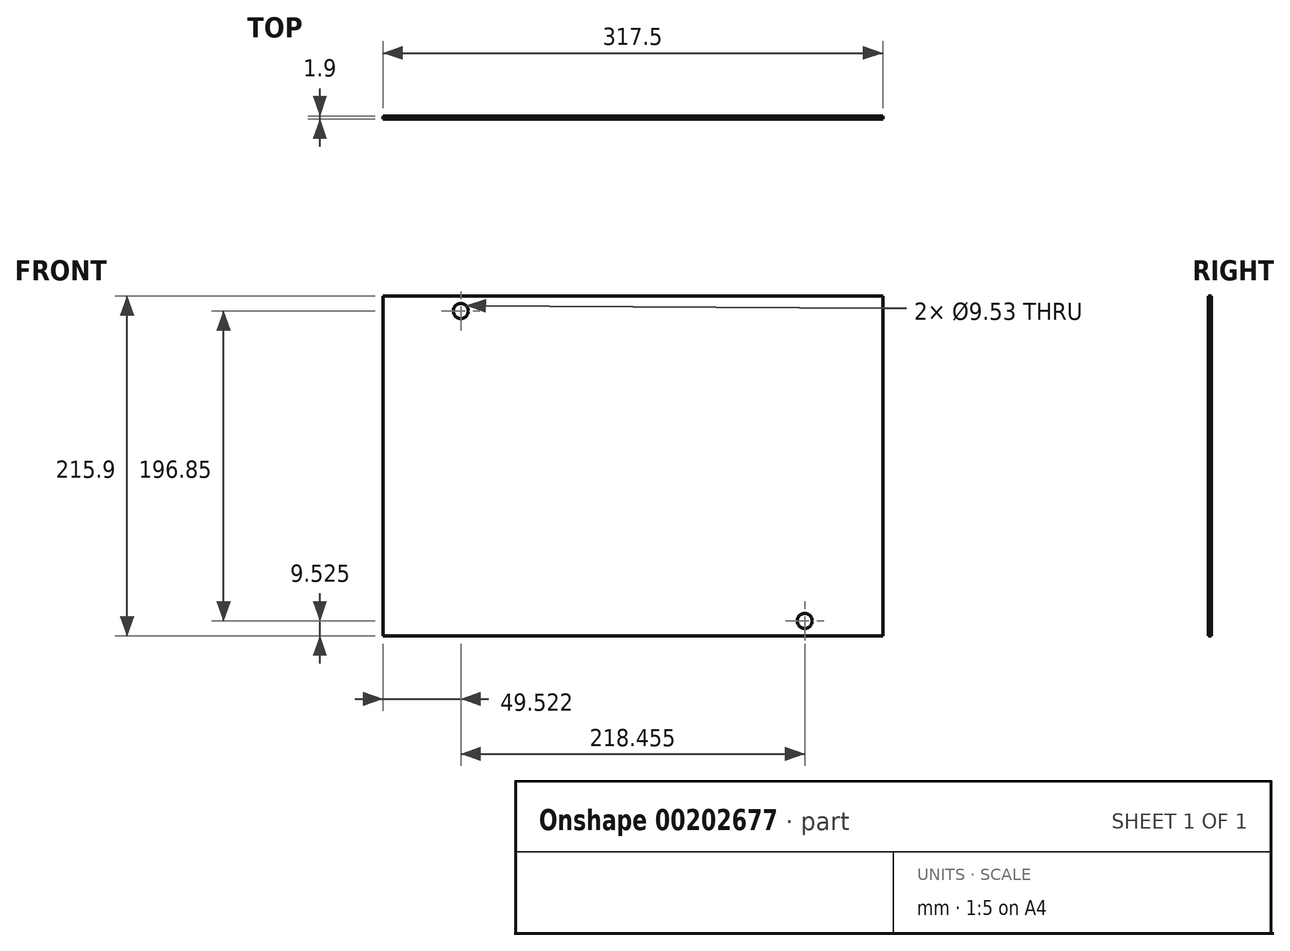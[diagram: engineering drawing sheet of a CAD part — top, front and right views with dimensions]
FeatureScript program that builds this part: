
annotation { "Feature Type Name" : "Feature", "Feature Type Description" : "" }
export const myFeature = defineFeature(function(context is Context, id is Id, definition is map)
    precondition{}
    {
        {
            var Q0;
            Q0=qCreatedBy(makeId("Front.planeOp"),FACE);
            var sketch = newSketch(context, id + "F0", { "sketchPlane" : qUnion([Q0])});
            skLineSegment(sketch, "E0.bottom", {"start": v(-158.75, 107.95) * mm, "end": v(158.75, 107.95) * mm});
            skLineSegment(sketch, "E0.top", {"start": v(-158.75, -107.95) * mm, "end": v(158.75, -107.95) * mm});
            skLineSegment(sketch, "E0.left", {"start": v(-158.75, 107.95) * mm, "end": v(-158.75, -107.95) * mm});
            skLineSegment(sketch, "E0.right", {"start": v(158.75, 107.95) * mm, "end": v(158.75, -107.95) * mm});
            skPoint(sketch, "E0.middle", {"position": v(0, 0) * mm});
            skSolve(sketch);
        }
        {
            var Q0;
            Q0 = qSketchRegion(id + "F0", true);
            extrude(context, id + "F1", {"entities" : qUnion([Q0]), "depth" : 1.9 * mm});
        }
        {
            var Q0;
            Q0=makeQuery(id+"F1.opExtrude","CAP_FACE",FACE,{"disambiguationData":[OSD([sQuery(id+"F0.wireOp",EDGE,"E0.bottom"),sQuery(id+"F0.wireOp",EDGE,"E0.top"),sQuery(id+"F0.wireOp",EDGE,"E0.left"),sQuery(id+"F0.wireOp",EDGE,"E0.right")])],"isStart":false});
            var sketch = newSketch(context, id + "F2", { "sketchPlane" : qUnion([Q0])});
            skCircle(sketch, "E1", {"center": v(-109.23, 98.42) * mm, "radius": 4.76 * mm});
            skCircle(sketch, "E2", {"center": v(109.23, -98.42) * mm, "radius": 4.76 * mm});
            skSolve(sketch);
        }
        {
            var Q0;
            Q0 = qSketchRegion(id + "F2", true);
            extrude(context, id + "F3", {"entities" : qUnion([Q0]), "operationType" : NewBodyOperationType.REMOVE, "oppositeDirection" : true, "depth" : 25.4 * mm});
        }
    });
